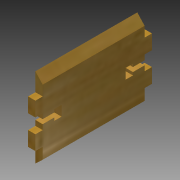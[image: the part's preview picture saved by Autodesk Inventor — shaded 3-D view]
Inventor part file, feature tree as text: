
AUTODESK INVENTOR PART (.ipt)
format: ipt  version: 2014 (Build 180170000, 170)  size: 155,136 bytes
history: native  units: mm
features: extrude x5, sketch x4
ambient origin geometry x8: Origin, YZ Plane, XZ Plane, XY Plane, X Axis, Y Axis, Z Axis, Center Point
bodies: Solid1 (feature_tree)
feature tree (9):
  extrude  "Extrusion1"  Depth=5.0mm
  extrude  "Extrusion2"  Depth=12.5mm
  sketch  "Sketch5"  dims[d9=10.0mm d10=10.0mm]
  extrude  "Extrusion3"  Depth=10.0mm
  extrude  "Extrusion4"  Depth=5.0mm TaperAngle=0.0deg
  extrude  "Extrusion5"  Depth=10.0mm
  sketch  "Sketch2"  dims[d0=5.0mm d1=54.829mm]
  sketch  "Sketch4"  dims[d2=70.0mm d3=0.0mm d8=12.5mm]
  sketch  "Sketch6"  dims[d11=10.0mm d12=5.0mm d13=0.0mm d20=10.0mm d21=10.0mm d22=10.0mm d23=12.5mm d24=54.829mm d25=12.329mm d26=5.0mm d27=0.0mm d28=5.504mm d29=4.688mm d30=70.0mm d31=0.0mm d35=1.5mm d36=8.0mm d37=2.0mm d38=5.0mm d39=2.0mm d41=5.0mm d42=0.0mm]
